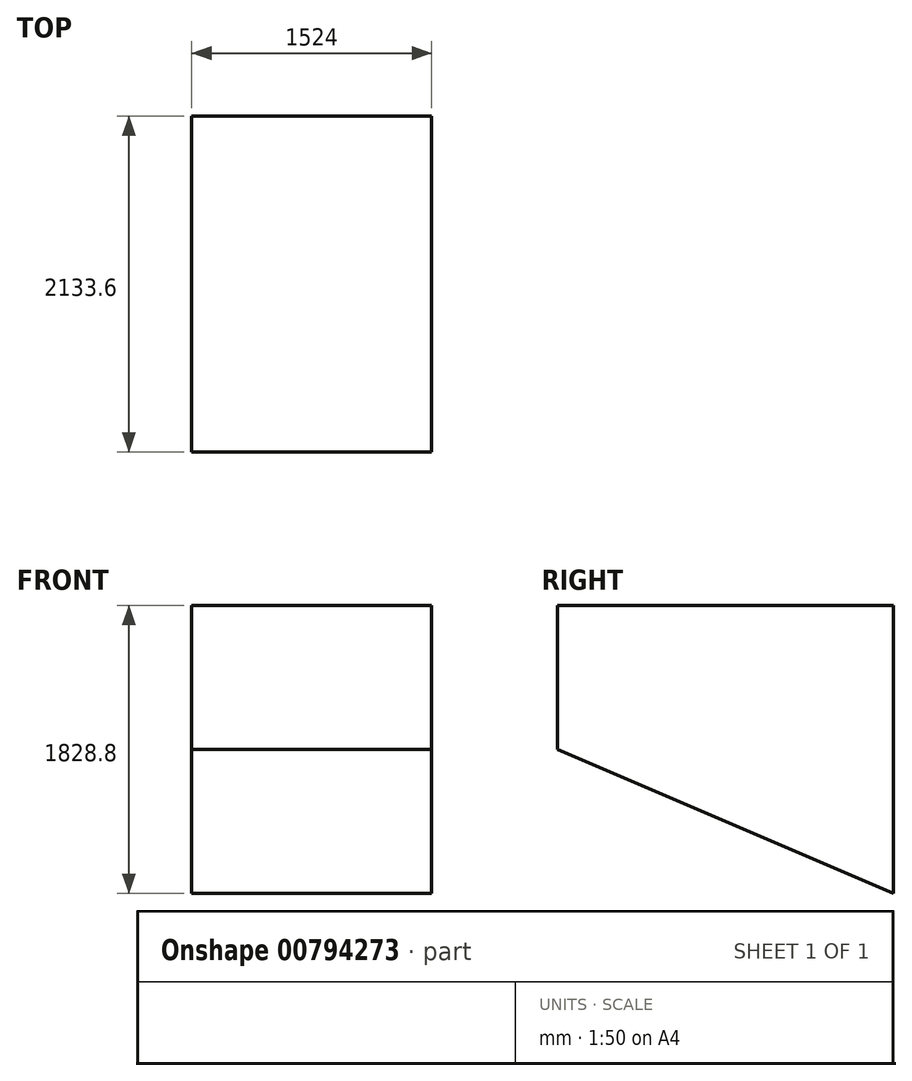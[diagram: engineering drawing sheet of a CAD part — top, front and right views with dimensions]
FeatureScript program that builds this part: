
annotation { "Feature Type Name" : "Feature", "Feature Type Description" : "" }
export const myFeature = defineFeature(function(context is Context, id is Id, definition is map)
    precondition{}
    {
        {
            var Q0;
            Q0=qCreatedBy(makeId("Right.planeOp"),FACE);
            var sketch = newSketch(context, id + "F0", { "sketchPlane" : qUnion([Q0])});
            skLineSegment(sketch, "E0", {"start": v(-1057.43, 1828.8) * mm, "end": v(1076.17, 1828.8) * mm});
            skLineSegment(sketch, "E1", {"start": v(1076.17, 1828.8) * mm, "end": v(1076.17, 0) * mm});
            skLineSegment(sketch, "E2", {"start": v(1076.17, 0) * mm, "end": v(-1057.43, 914.4) * mm});
            skLineSegment(sketch, "E3", {"start": v(-1057.43, 914.4) * mm, "end": v(-1057.43, 1828.8) * mm});
            skSolve(sketch);
        }
        {
            var Q0;
            Q0=makeQuery(id+"F0.imprint","IMPRINT",FACE,{"disambiguationData":[TD([[makeQuery(id+"F0.imprint","IMPRINT",EDGE,{"derivedFrom":sQuery(id+"F0.wireOp",EDGE,"E0")}),-1.0]])]});
            extrude(context, id + "F1", {"entities" : qUnion([Q0]), "depth" : 1524 * mm, "offsetDistance" : 30.48 * mm});
        }
    });
